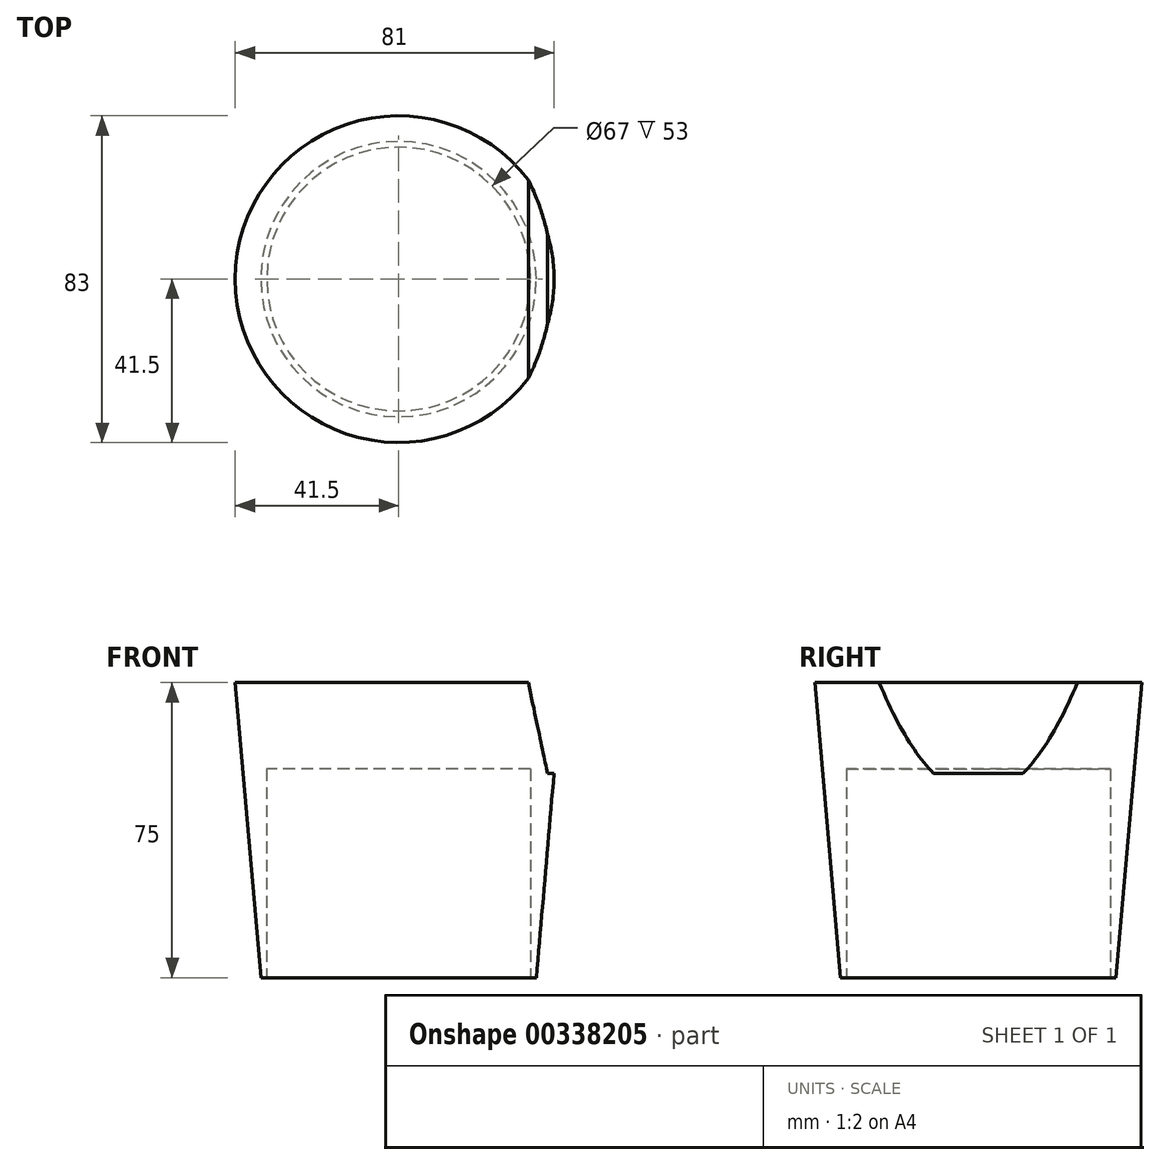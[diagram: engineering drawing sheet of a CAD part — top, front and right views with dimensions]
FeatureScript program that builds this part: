
annotation { "Feature Type Name" : "Feature", "Feature Type Description" : "" }
export const myFeature = defineFeature(function(context is Context, id is Id, definition is map)
    precondition{}
    {
        {
            var Q0;
            Q0=qCreatedBy(makeId("Top.planeOp"),FACE);
            var sketch = newSketch(context, id + "F0", { "sketchPlane" : qUnion([Q0])});
            skCircle(sketch, "E0", {"center": v(0, 0) * mm, "radius": 35 * mm});
            skSolve(sketch);
        }
        {
            var Q0;
            Q0=qCreatedBy(makeId("Top.planeOp"),FACE);
            cPlane(context, id + "F1", {"entities" : qUnion([Q0]), "cplaneType" : CPlaneType.OFFSET, "offset" : 75 * mm, "width" : 150 * mm, "height" : 150 * mm});
        }
        {
            var Q0;
            Q0=qCreatedBy(id+"F1.planeOp",FACE);
            var sketch = newSketch(context, id + "F2", { "sketchPlane" : qUnion([Q0])});
            skCircle(sketch, "E1", {"center": v(0, 0) * mm, "radius": 41.5 * mm});
            skSolve(sketch);
        }
        {
            var Q0;
            Q0=makeQuery(id+"F2.imprint","IMPRINT",FACE,{"disambiguationData":[TD([[makeQuery(id+"F2.imprint","IMPRINT",EDGE,{"derivedFrom":sQuery(id+"F2.wireOp",EDGE,"E1")}),1.0]])]});
            var Q1;
            Q1=makeQuery(id+"F0.imprint","IMPRINT",FACE,{"disambiguationData":[TD([[makeQuery(id+"F0.imprint","IMPRINT",EDGE,{"derivedFrom":sQuery(id+"F0.wireOp",EDGE,"E0")}),1.0]])]});
            loft(context, id + "F3", {"sheetProfilesArray" : [{ "sheetProfileEntities" : qUnion([Q0]) }, { "sheetProfileEntities" : qUnion([Q1]) }]});
        }
        {
            var Q0;
            Q0=qCreatedBy(makeId("Top.planeOp"),FACE);
            cPlane(context, id + "F4", {"entities" : qUnion([Q0]), "cplaneType" : CPlaneType.OFFSET, "offset" : 50 * mm, "width" : 150 * mm, "height" : 150 * mm});
        }
        {
            var Q0;
            Q0=qCreatedBy(makeId("Front.planeOp"),FACE);
            var sketch = newSketch(context, id + "F5", { "sketchPlane" : qUnion([Q0])});
            skLineSegment(sketch, "E2", {"start": v(37.83, 51.9) * mm, "end": v(40.55, 51.9) * mm});
            skLineSegment(sketch, "E3", {"start": v(40.55, 51.9) * mm, "end": v(42.3, 75) * mm});
            skLineSegment(sketch, "E4", {"start": v(42.3, 75) * mm, "end": v(32.98, 75) * mm});
            skLineSegment(sketch, "E5", {"start": v(32.98, 75) * mm, "end": v(37.83, 51.9) * mm});
            skSolve(sketch);
        }
        {
            var Q0;
            Q0 = qSketchRegion(id + "F5", true);
            extrude(context, id + "F6", {"entities" : qUnion([Q0]), "operationType" : NewBodyOperationType.REMOVE, "endBound" : BoundingType.SYMMETRIC, "oppositeDirection" : true, "depth" : 55 * mm});
        }
        {
            var Q0;
            Q0=qCreatedBy(makeId("Top.planeOp"),FACE);
            var sketch = newSketch(context, id + "F7", { "sketchPlane" : qUnion([Q0])});
            skCircle(sketch, "E6", {"center": v(0, 0) * mm, "radius": 33.5 * mm});
            skSolve(sketch);
        }
        {
            var Q0;
            Q0 = qSketchRegion(id + "F7", true);
            extrude(context, id + "F8", {"entities" : qUnion([Q0]), "operationType" : NewBodyOperationType.REMOVE, "depth" : 53 * mm});
        }
    });
